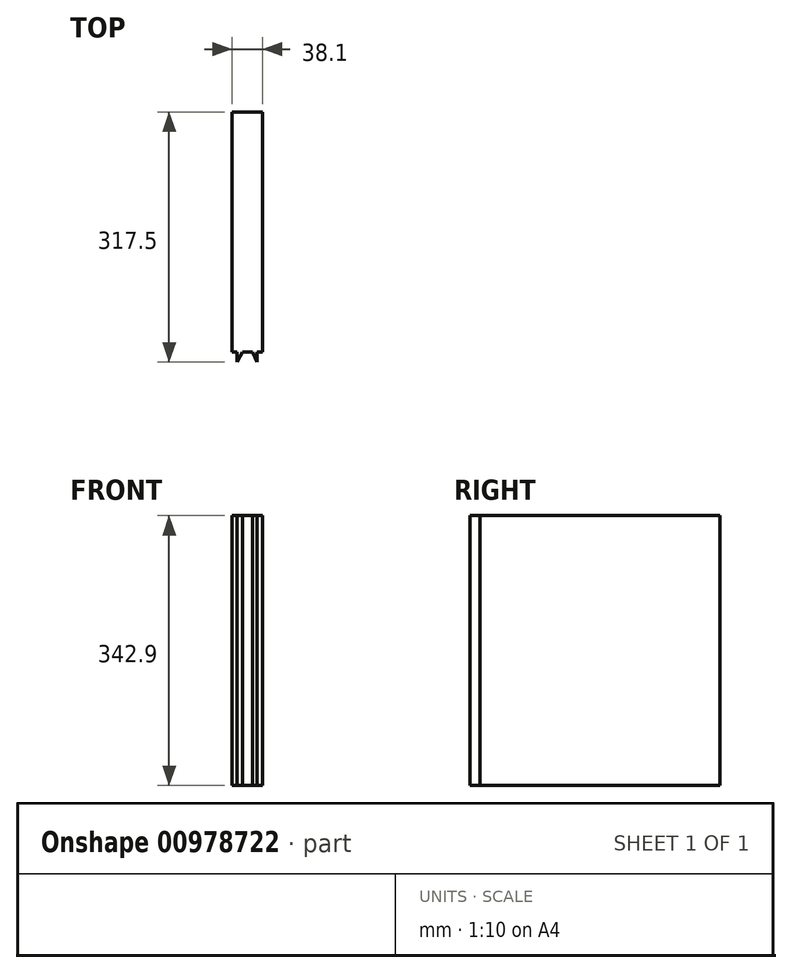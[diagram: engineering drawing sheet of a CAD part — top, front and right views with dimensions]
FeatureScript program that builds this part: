
annotation { "Feature Type Name" : "Feature", "Feature Type Description" : "" }
export const myFeature = defineFeature(function(context is Context, id is Id, definition is map)
    precondition{}
    {
        {
            var Q0;
            Q0=qCreatedBy(makeId("Front.planeOp"),FACE);
            var sketch = newSketch(context, id + "F0", { "sketchPlane" : qUnion([Q0])});
            skLineSegment(sketch, "E0.bottom", {"start": v(-19.05, 171.45) * mm, "end": v(19.05, 171.45) * mm});
            skLineSegment(sketch, "E0.top", {"start": v(-19.05, -171.45) * mm, "end": v(19.05, -171.45) * mm});
            skLineSegment(sketch, "E0.left", {"start": v(-19.05, 171.45) * mm, "end": v(-19.05, -171.45) * mm});
            skLineSegment(sketch, "E0.right", {"start": v(19.05, 171.45) * mm, "end": v(19.05, -171.45) * mm});
            skPoint(sketch, "E0.middle", {"position": v(0, 0) * mm});
            skSolve(sketch);
        }
        {
            var Q0;
            Q0=makeQuery(id+"F0.imprint","IMPRINT",FACE,{"disambiguationData":[TD([[makeQuery(id+"F0.imprint","IMPRINT",EDGE,{"derivedFrom":sQuery(id+"F0.wireOp",EDGE,"E0.bottom")}),-1.0]])]});
            extrude(context, id + "F1", {"entities" : qUnion([Q0]), "depth" : 304.8 * mm, "offsetDistance" : 25.4 * mm});
        }
        {
            var Q0;
            Q0=makeQuery(id+"F1.opExtrude","SWEPT_FACE",FACE,{"disambiguationData":[OSD([sQuery(id+"F0.wireOp",EDGE,"E0.top")])]});
            var sketch = newSketch(context, id + "F2", { "sketchPlane" : qUnion([Q0])});
            skLineSegment(sketch, "E1.bottom", {"start": v(-12.7, 304.8) * mm, "end": v(12.7, 304.8) * mm});
            skLineSegment(sketch, "E1.top", {"start": v(-12.7, 317.5) * mm, "end": v(12.7, 317.5) * mm});
            skLineSegment(sketch, "E1.left", {"start": v(-12.7, 304.8) * mm, "end": v(-12.7, 317.5) * mm});
            skLineSegment(sketch, "E1.right", {"start": v(12.7, 304.8) * mm, "end": v(12.7, 317.5) * mm});
            skLineSegment(sketch, "E2", {"start": v(-12.7, 317.5) * mm, "end": v(-6.35, 304.8) * mm});
            skLineSegment(sketch, "E3", {"start": v(-6.35, 304.8) * mm, "end": v(-12.7, 304.8) * mm});
            skLineSegment(sketch, "E4", {"start": v(12.7, 317.5) * mm, "end": v(6.35, 304.8) * mm});
            skLineSegment(sketch, "E5", {"start": v(6.35, 304.8) * mm, "end": v(12.7, 304.8) * mm});
            skSolve(sketch);
        }
        {
            var Q0;
            {var subQ1=sQuery(id+"F2.wireOp",EDGE,"E1.bottom");Q0=makeQuery(id+"F2.imprint","IMPRINT",FACE,{"disambiguationData":[TD([[makeQuery(id+"F2.imprint","IMPRINT",EDGE,{"derivedFrom":subQ1}),1.0]])]});}
            extrude(context, id + "F3", {"entities" : qUnion([Q0]), "operationType" : NewBodyOperationType.ADD, "oppositeDirection" : true, "depth" : 342.9 * mm, "offsetDistance" : 25.4 * mm});
        }
    });
